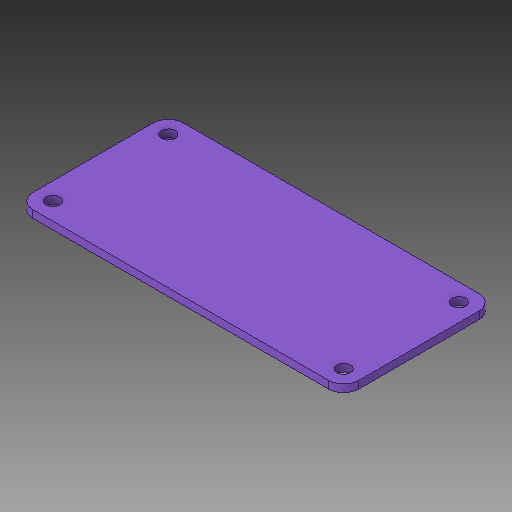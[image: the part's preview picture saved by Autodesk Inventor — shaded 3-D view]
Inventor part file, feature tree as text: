
AUTODESK INVENTOR PART (.ipt)
format: ipt  version: 2019.2 (Build 232265000, 265)  size: 110,592 bytes
history: native  units: in
note: dims shown in document units (in); Inventor stores cm internally (conversion verified against a paired STEP export)
features: sketch x2, extrude x1, hole x1, fillet x1
ambient origin geometry x8: Origin, YZ Plane, XZ Plane, XY Plane, X Axis, Y Axis, Z Axis, Center Point
bodies: Solid1 (feature_tree)
feature tree (5):
  extrude  "Extrusion1"  Depth=1.1811in
  hole  "Hole1"  [1 undecoded]
  fillet  "Fillet1"  Radius=0.9055in
  sketch  "Sketch1"  dims[d0=2.5591in d1=1.1811in]
  sketch  "Sketch2"  dims[d4=0.0591in d5=0.0in d6=2.2835in d7=0.9055in d8=0.1083in d9=0.75in d10=0.375in d11=0.25in d12=0.5635in d13=1.0in d14=0.8108in d15=0.1181in]
note: 1 required parameter value undecoded (feature->parameter linkage not recoverable at this tier; creation-order binding heuristic only, values carry confidence <= 0.55)
